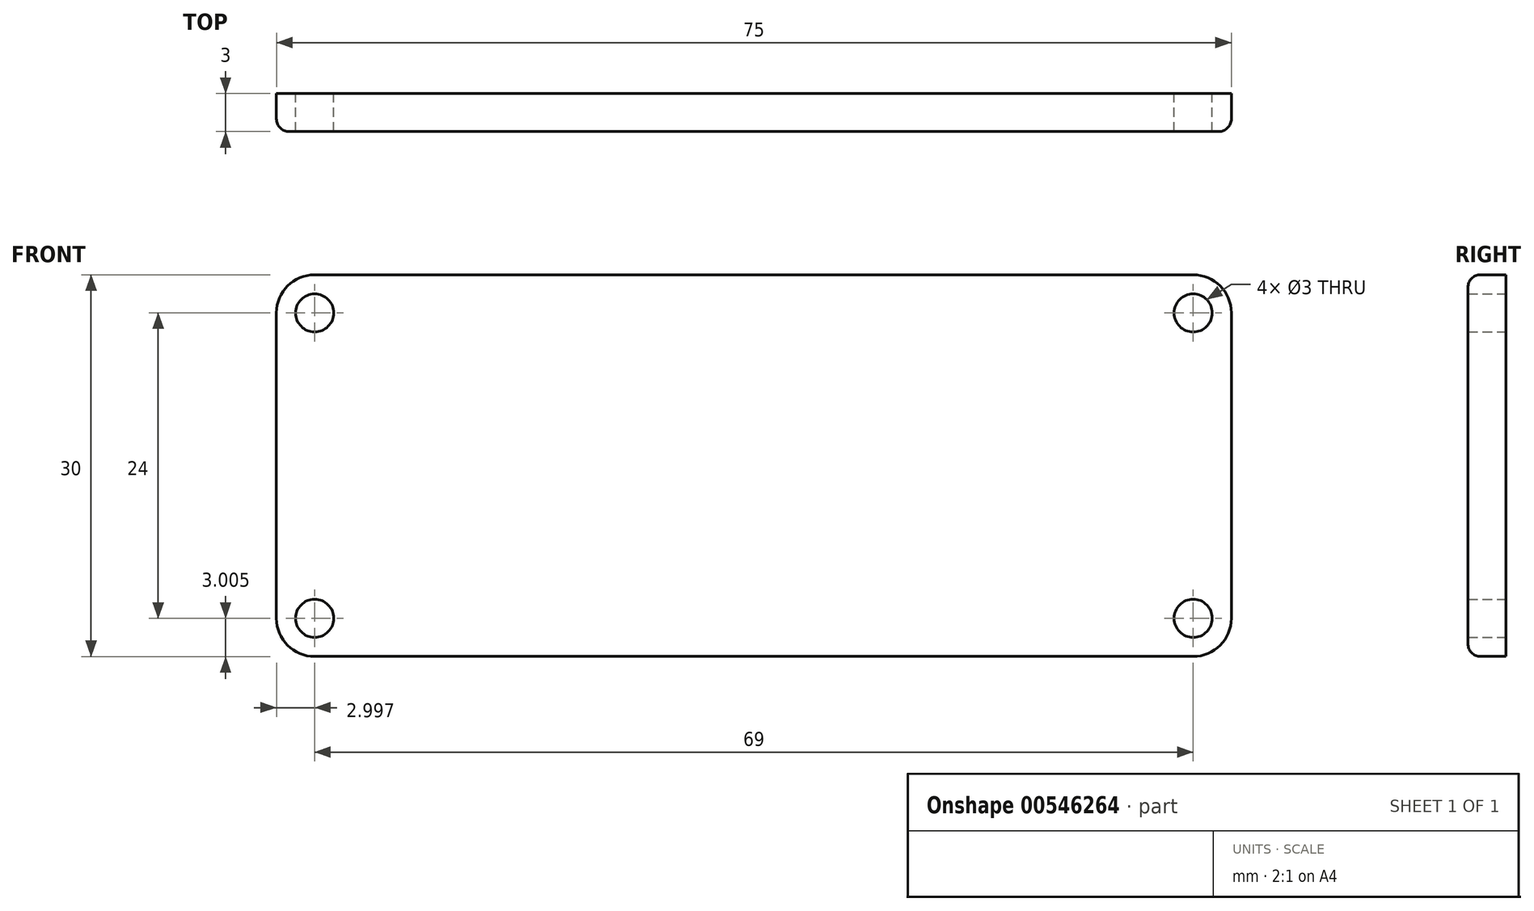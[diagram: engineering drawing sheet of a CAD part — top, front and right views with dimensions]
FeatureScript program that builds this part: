
annotation { "Feature Type Name" : "Feature", "Feature Type Description" : "" }
export const myFeature = defineFeature(function(context is Context, id is Id, definition is map)
    precondition{}
    {
        {
            var Q0;
            Q0=qCreatedBy(makeId("Front.planeOp"),FACE);
            var sketch = newSketch(context, id + "F0", { "sketchPlane" : qUnion([Q0])});
            skLineSegment(sketch, "E0.bottom", {"start": v(-33.95, 11.33) * mm, "end": v(35.05, 11.33) * mm});
            skLineSegment(sketch, "E0.top", {"start": v(-33.95, -18.67) * mm, "end": v(35.05, -18.67) * mm});
            skLineSegment(sketch, "E0.left", {"start": v(-36.95, 8.33) * mm, "end": v(-36.95, -15.67) * mm});
            skLineSegment(sketch, "E0.right", {"start": v(38.05, 8.33) * mm, "end": v(38.05, -15.67) * mm});
            skPoint(sketch, "E1.visualSharp", {"position": v(-36.95, 11.33) * mm});
            skArc(sketch, "E1.filletArc", {"start": v(-33.95, 11.33) * mm, "mid": v(-36.07, 10.46) * mm, "end": v(-36.95, 8.33) * mm});
            skPoint(sketch, "E2.visualSharp", {"position": v(-36.95, -18.67) * mm});
            skArc(sketch, "E2.filletArc", {"start": v(-36.95, -15.67) * mm, "mid": v(-36.07, -17.79) * mm, "end": v(-33.95, -18.67) * mm});
            skPoint(sketch, "E3.visualSharp", {"position": v(38.05, -18.67) * mm});
            skArc(sketch, "E3.filletArc", {"start": v(35.05, -18.67) * mm, "mid": v(37.17, -17.79) * mm, "end": v(38.05, -15.67) * mm});
            skPoint(sketch, "E4.visualSharp", {"position": v(38.05, 11.33) * mm});
            skArc(sketch, "E4.filletArc", {"start": v(38.05, 8.33) * mm, "mid": v(37.17, 10.46) * mm, "end": v(35.05, 11.33) * mm});
            skCircle(sketch, "E5", {"center": v(-33.95, 8.33) * mm, "radius": 1.5 * mm});
            skCircle(sketch, "E6", {"center": v(-33.95, -15.67) * mm, "radius": 1.5 * mm});
            skCircle(sketch, "E7", {"center": v(35.05, 8.33) * mm, "radius": 1.5 * mm});
            skCircle(sketch, "E8", {"center": v(35.05, -15.67) * mm, "radius": 1.5 * mm});
            skSolve(sketch);
        }
        {
            var Q0;
            Q0 = qSketchRegion(id + "F0", true);
            extrude(context, id + "F1", {"entities" : qUnion([Q0]), "depth" : 3 * mm, "offsetDistance" : 25 * mm});
        }
        {
            var Q0;
            Q0=makeQuery(id+"F1.opExtrude","CAP_EDGE",EDGE,{"disambiguationData":[OSD([sQuery(id+"F0.wireOp",EDGE,"E0.bottom")])],"isStart":false});
            var Q1;
            Q1=makeQuery(id+"F1.opExtrude","CAP_EDGE",EDGE,{"disambiguationData":[OSD([sQuery(id+"F0.wireOp",EDGE,"E1.filletArc")])],"isStart":false});
            var Q2;
            Q2=makeQuery(id+"F1.opExtrude","CAP_EDGE",EDGE,{"disambiguationData":[OSD([sQuery(id+"F0.wireOp",EDGE,"E0.left")])],"isStart":false});
            var Q3;
            Q3=makeQuery(id+"F1.opExtrude","CAP_EDGE",EDGE,{"disambiguationData":[OSD([sQuery(id+"F0.wireOp",EDGE,"E2.filletArc")])],"isStart":false});
            var Q4;
            Q4=makeQuery(id+"F1.opExtrude","CAP_EDGE",EDGE,{"disambiguationData":[OSD([sQuery(id+"F0.wireOp",EDGE,"E0.top")])],"isStart":false});
            var Q5;
            Q5=makeQuery(id+"F1.opExtrude","CAP_EDGE",EDGE,{"disambiguationData":[OSD([sQuery(id+"F0.wireOp",EDGE,"E4.filletArc")])],"isStart":false});
            var Q6;
            Q6=makeQuery(id+"F1.opExtrude","CAP_EDGE",EDGE,{"disambiguationData":[OSD([sQuery(id+"F0.wireOp",EDGE,"E0.right")])],"isStart":false});
            var Q7;
            Q7=makeQuery(id+"F1.opExtrude","CAP_EDGE",EDGE,{"disambiguationData":[OSD([sQuery(id+"F0.wireOp",EDGE,"E3.filletArc")])],"isStart":false});
            fillet(context, id + "F2", {"entities" : qUnion([Q0, Q1, Q2, Q3, Q4, Q5, Q6, Q7]), "tangentPropagation" : true, "radius" : 1 * mm, "defaultsChanged" : true, "vertexSettings" : [], "allowEdgeOverflow" : false});
        }
    });
